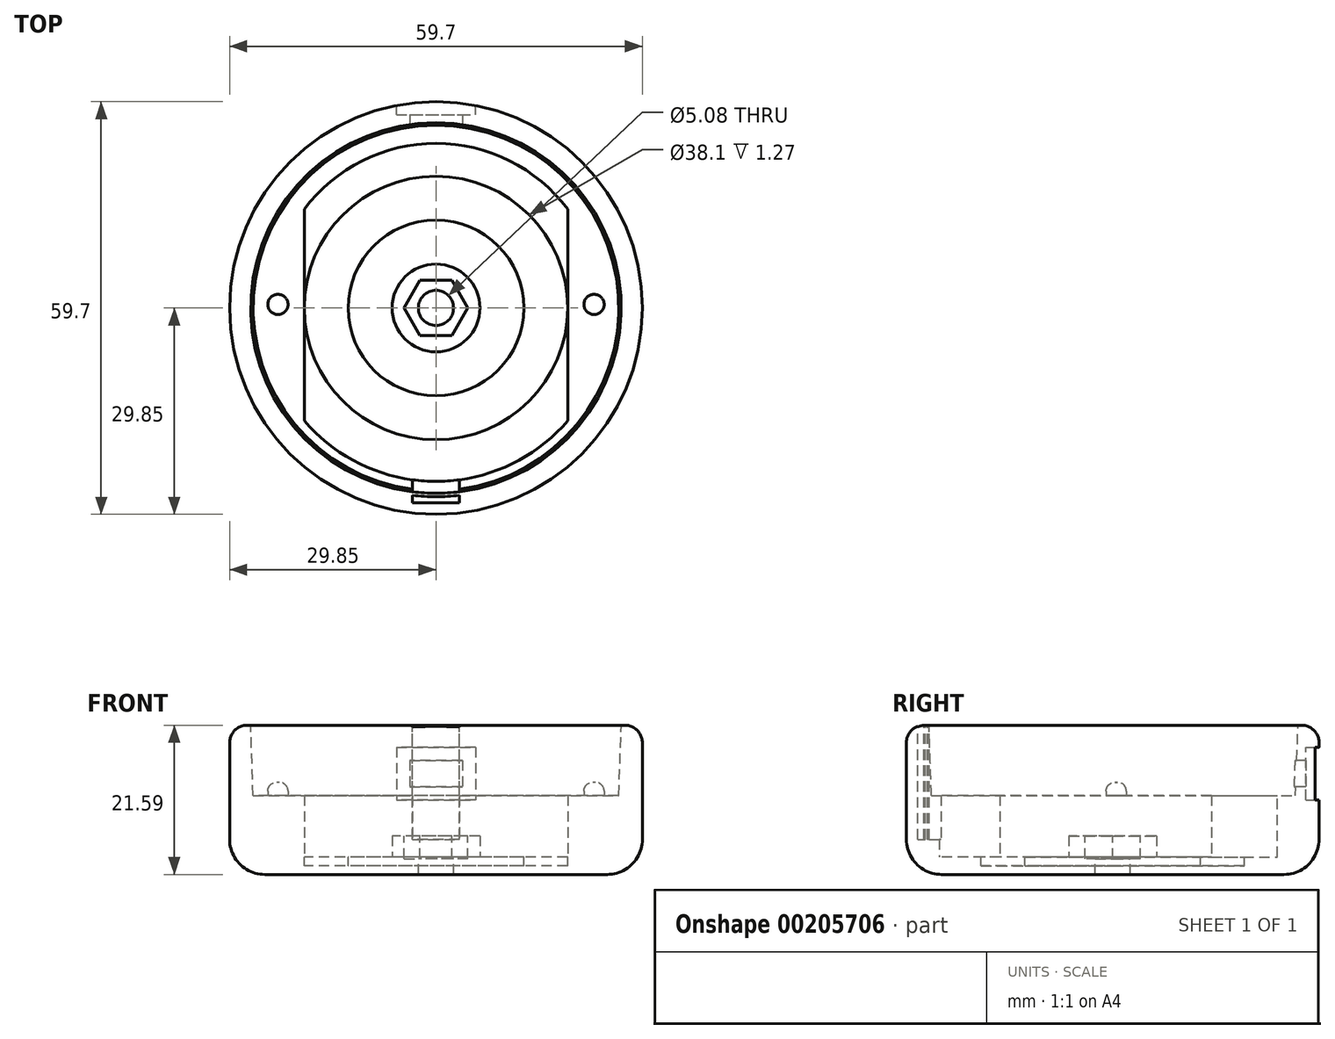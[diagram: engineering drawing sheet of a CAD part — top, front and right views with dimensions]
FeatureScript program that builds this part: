
annotation { "Feature Type Name" : "Feature", "Feature Type Description" : "" }
export const myFeature = defineFeature(function(context is Context, id is Id, definition is map)
    precondition{}
    {
        {
            var Q0;
            Q0=qCreatedBy(makeId("Top.planeOp"),FACE);
            var sketch = newSketch(context, id + "F0", { "sketchPlane" : qUnion([Q0])});
            skCircle(sketch, "E0", {"center": v(0, 0) * mm, "radius": 29.84 * mm});
            skSolve(sketch);
        }
        {
            var Q0;
            Q0 = qSketchRegion(id + "F0", true);
            extrude(context, id + "F1", {"entities" : qUnion([Q0]), "depth" : 21.59 * mm});
        }
        {
            var Q0;
            Q0=makeQuery(id+"F1.opExtrude","CAP_FACE",FACE,{"disambiguationData":[OSD([sQuery(id+"F0.wireOp",EDGE,"E0")])],"isStart":false});
            var sketch = newSketch(context, id + "F2", { "sketchPlane" : qUnion([Q0])});
            skCircle(sketch, "E1", {"center": v(0, 0) * mm, "radius": 26.8 * mm});
            skSolve(sketch);
        }
        {
            var Q0;
            Q0=makeQuery(id+"F2.imprint","IMPRINT",FACE,{"disambiguationData":[TD([[makeQuery(id+"F2.imprint","IMPRINT",EDGE,{"derivedFrom":sQuery(id+"F2.wireOp",EDGE,"E1")}),1.0]])]});
            extrude(context, id + "F3", {"entities" : qUnion([Q0]), "operationType" : NewBodyOperationType.REMOVE, "oppositeDirection" : true, "depth" : 10.16 * mm, "hasDraft" : true, "draftAngle" : 2 * degree, "draftPullDirection" : true});
        }
        {
            var Q0;
            Q0=makeQuery(id+"F3.boolean.opBoolean","COPY",FACE,{"derivedFrom":makeQuery(id+"F3.opExtrude","CAP_FACE",FACE,{"disambiguationData":[OSD([sQuery(id+"F2.wireOp",EDGE,"E1")])],"isStart":false})});
            var sketch = newSketch(context, id + "F4", { "sketchPlane" : qUnion([Q0])});
            skCircle(sketch, "E2", {"center": v(0, 0) * mm, "radius": 23.81 * mm});
            skSolve(sketch);
        }
        {
            var Q0;
            Q0 = qSketchRegion(id + "F4", true);
            extrude(context, id + "F5", {"entities" : qUnion([Q0]), "operationType" : NewBodyOperationType.REMOVE, "oppositeDirection" : true, "depth" : 8.9 * mm});
        }
        {
            var Q0;
            Q0=makeQuery(id+"F5.boolean.opBoolean","COPY",FACE,{"derivedFrom":makeQuery(id+"F5.opExtrude","CAP_FACE",FACE,{"disambiguationData":[OSD([sQuery(id+"F4.wireOp",EDGE,"E2")])],"isStart":false})});
            var sketch = newSketch(context, id + "F6", { "sketchPlane" : qUnion([Q0])});
            skCircle(sketch, "E3", {"center": v(0, 0) * mm, "radius": 6.35 * mm});
            skSolve(sketch);
        }
        {
            var Q0;
            Q0 = qSketchRegion(id + "F6", true);
            extrude(context, id + "F7", {"entities" : qUnion([Q0]), "operationType" : NewBodyOperationType.ADD, "depth" : 3.05 * mm});
        }
        {
            var Q0;
            Q0=makeQuery(id+"F7.opExtrude","CAP_FACE",FACE,{"disambiguationData":[OSD([sQuery(id+"F6.wireOp",EDGE,"E3")])],"isStart":false});
            var sketch = newSketch(context, id + "F8", { "sketchPlane" : qUnion([Q0])});
            skCircle(sketch, "E4", {"center": v(0, 0) * mm, "radius": 2.54 * mm});
            skSolve(sketch);
        }
        {
            var Q0;
            Q0=makeQuery(id+"F8.imprint","IMPRINT",FACE,{"disambiguationData":[TD([[makeQuery(id+"F8.imprint","IMPRINT",EDGE,{"derivedFrom":sQuery(id+"F8.wireOp",EDGE,"E4")}),1.0]])]});
            extrude(context, id + "F9", {"entities" : qUnion([Q0]), "operationType" : NewBodyOperationType.REMOVE, "oppositeDirection" : true, "depth" : 25.4 * mm});
        }
        {
            var Q0;
            Q0=makeQuery(id+"F7.opExtrude","CAP_FACE",FACE,{"disambiguationData":[OSD([sQuery(id+"F6.wireOp",EDGE,"E3")])],"isStart":false});
            cPlane(context, id + "F10", {"entities" : qUnion([Q0]), "cplaneType" : CPlaneType.OFFSET, "offset" : 0 * mm, "oppositeDirection" : true, "width" : 152.4 * mm, "height" : 152.4 * mm});
        }
        {
            var Q0;
            Q0=qCreatedBy(id+"F10.planeOp",FACE);
            var sketch = newSketch(context, id + "F11", { "sketchPlane" : qUnion([Q0])});
            skCircle(sketch, "E5.cCircle", {"center": v(0, 0) * mm, "radius": 4.62 * mm, "construction": true});
            skLineSegment(sketch, "E5.0", {"start": v(2.3, -4) * mm, "end": v(-2.3, -4) * mm});
            skLineSegment(sketch, "E5.1", {"start": v(-2.3, -4) * mm, "end": v(-4.62, 0) * mm});
            skLineSegment(sketch, "E5.2", {"start": v(-4.62, 0) * mm, "end": v(-2.3, 4) * mm});
            skLineSegment(sketch, "E5.3", {"start": v(-2.3, 4) * mm, "end": v(2.3, 4) * mm});
            skLineSegment(sketch, "E5.4", {"start": v(2.3, 4) * mm, "end": v(4.62, 0) * mm});
            skLineSegment(sketch, "E5.5", {"start": v(4.62, 0) * mm, "end": v(2.3, -4) * mm});
            skSolve(sketch);
        }
        {
            var Q0;
            Q0 = qSketchRegion(id + "F11", true);
            extrude(context, id + "F12", {"entities" : qUnion([Q0]), "operationType" : NewBodyOperationType.REMOVE, "oppositeDirection" : true, "depth" : 3.3 * mm});
        }
        {
            var Q0;
            Q0=makeQuery(id+"F1.opExtrude","CAP_EDGE",EDGE,{"disambiguationData":[OSD([sQuery(id+"F0.wireOp",EDGE,"E0")])],"isStart":true});
            fillet(context, id + "F13", {"entities" : qUnion([Q0]), "radius" : 5.08 * mm, "tangentPropagation" : true, "allowEdgeOverflow" : false});
        }
        {
            var Q0;
            Q0=makeQuery(id+"F1.opExtrude","CAP_EDGE",EDGE,{"disambiguationData":[OSD([sQuery(id+"F0.wireOp",EDGE,"E0")])],"isStart":false});
            fillet(context, id + "F14", {"entities" : qUnion([Q0]), "radius" : 2.54 * mm, "tangentPropagation" : true, "allowEdgeOverflow" : false});
        }
        {
            var Q0;
            Q0=makeQuery(id+"F5.boolean.opBoolean","COPY",FACE,{"derivedFrom":makeQuery(id+"F5.opExtrude","CAP_FACE",FACE,{"disambiguationData":[OSD([sQuery(id+"F4.wireOp",EDGE,"E2")])],"isStart":false})});
            var sketch = newSketch(context, id + "F15", { "sketchPlane" : qUnion([Q0])});
            skCircle(sketch, "E6", {"center": v(0, 0) * mm, "radius": 19.05 * mm});
            skCircle(sketch, "E7", {"center": v(0, 0) * mm, "radius": 12.7 * mm});
            skSolve(sketch);
        }
        {
            var Q0;
            Q0 = qSketchRegion(id + "F15", true);
            extrude(context, id + "F16", {"entities" : qUnion([Q0]), "operationType" : NewBodyOperationType.REMOVE, "oppositeDirection" : true, "depth" : 1.27 * mm});
        }
        {
            var Q0;
            {var subQ0=sQuery(id+"F4.wireOp",EDGE,"E2");Q0=makeQuery(id+"F16.boolean.opBoolean","SPLIT",FACE,{"disambiguationData":[TD([makeQuery(id+"F5.boolean.opBoolean","COPY",FACE,{"derivedFrom":makeQuery(id+"F5.opExtrude","SWEPT_FACE",FACE,{"disambiguationData":[OSD([subQ0])]})})])],"derivedFrom":makeQuery(id+"F5.boolean.opBoolean","COPY",FACE,{"derivedFrom":makeQuery(id+"F5.opExtrude","CAP_FACE",FACE,{"disambiguationData":[OSD([subQ0])],"isStart":false})})});}
            var sketch = newSketch(context, id + "F17", { "sketchPlane" : qUnion([Q0])});
            skLineSegment(sketch, "E8", {"start": v(-19.05, 14.29) * mm, "end": v(-19.05, -14.29) * mm});
            skArc(sketch, "E9", {"start": v(-19.05, 14.29) * mm, "mid": v(-23.81, 0) * mm, "end": v(-19.05, -14.29) * mm});
            skLineSegment(sketch, "E10", {"start": v(19.05, 14.29) * mm, "end": v(19.05, -14.29) * mm});
            skArc(sketch, "E11", {"start": v(19.05, -14.29) * mm, "mid": v(23.81, 0) * mm, "end": v(19.05, 14.29) * mm});
            skSolve(sketch);
        }
        {
            var Q0;
            {var subQ0=sQuery(id+"F17.wireOp",EDGE,"E9");Q0=makeQuery(id+"F17.imprint","IMPRINT",FACE,{"disambiguationData":[TD([[makeQuery(id+"F17.imprint","IMPRINT",EDGE,{"derivedFrom":subQ0}),1.0]])]});}
            var Q1;
            {var subQ0=sQuery(id+"F17.wireOp",EDGE,"E11");Q1=makeQuery(id+"F17.imprint","IMPRINT",FACE,{"disambiguationData":[TD([[makeQuery(id+"F17.imprint","IMPRINT",EDGE,{"derivedFrom":subQ0}),1.0]])]});}
            var Q2;
            Q2=makeQuery(id+"F3.boolean.opBoolean","COPY",FACE,{"derivedFrom":makeQuery(id+"F3.opExtrude","CAP_FACE",FACE,{"disambiguationData":[OSD([sQuery(id+"F2.wireOp",EDGE,"E1")])],"isStart":false})});
            extrude(context, id + "F18", {"entities" : qUnion([Q0, Q1]), "operationType" : NewBodyOperationType.ADD, "endBound" : BoundingType.UP_TO_SURFACE, "endBoundEntityFace" : qUnion([Q2]), "depth" : 25.4 * mm});
        }
        {
            var Q0;
            {var subQ0=sQuery(id+"F2.wireOp",EDGE,"E1");Q0=makeQuery(id+"F18.boolean.opBoolean","MERGE",FACE,{"derivedFrom":[makeQuery(id+"F3.boolean.opBoolean","COPY",FACE,{"derivedFrom":makeQuery(id+"F3.opExtrude","CAP_FACE",FACE,{"disambiguationData":[OSD([subQ0])],"isStart":false})}),makeQuery(id+"F18.opExtrude","CAP_FACE",FACE,{"disambiguationData":[OSD([subQ0]),ownerDisambiguation([makeQuery(id+"F18.opExtrude","SWEPT_BODY",BODY,{"disambiguationData":[OSD([sQuery(id+"F17.wireOp",EDGE,"E8"),sQuery(id+"F17.wireOp",EDGE,"E9")])]})])],"isStart":false}),makeQuery(id+"F18.opExtrude","CAP_FACE",FACE,{"disambiguationData":[OSD([subQ0]),ownerDisambiguation([makeQuery(id+"F18.opExtrude","SWEPT_BODY",BODY,{"disambiguationData":[OSD([sQuery(id+"F17.wireOp",EDGE,"E10"),sQuery(id+"F17.wireOp",EDGE,"E11")])]})])],"isStart":false})]});}
            var sketch = newSketch(context, id + "F19", { "sketchPlane" : qUnion([Q0])});
            skCircle(sketch, "E12", {"center": v(-22.86, 0.5) * mm, "radius": 1.46 * mm});
            skCircle(sketch, "E13", {"center": v(22.86, 0.5) * mm, "radius": 1.46 * mm});
            skSolve(sketch);
        }
        {
            var Q0;
            Q0 = qSketchRegion(id + "F19", true);
            extrude(context, id + "F20", {"entities" : qUnion([Q0]), "operationType" : NewBodyOperationType.ADD, "depth" : 1.9 * mm});
        }
        {
            var Q0;
            Q0=makeQuery(id+"F20.opExtrude","CAP_EDGE",EDGE,{"disambiguationData":[OSD([sQuery(id+"F19.wireOp",EDGE,"E12")])],"isStart":false});
            var Q1;
            Q1=makeQuery(id+"F20.opExtrude","CAP_EDGE",EDGE,{"disambiguationData":[OSD([sQuery(id+"F19.wireOp",EDGE,"E13")])],"isStart":false});
            fillet(context, id + "F21", {"entities" : qUnion([Q0, Q1]), "radius" : 1.27 * mm, "tangentPropagation" : true, "allowEdgeOverflow" : false});
        }
        {
            var Q0;
            Q0=qCreatedBy(makeId("Front.planeOp"),FACE);
            var sketch = newSketch(context, id + "F22", { "sketchPlane" : qUnion([Q0])});
            skLineSegment(sketch, "E14.bottom", {"start": v(3.8, 12.7) * mm, "end": v(-3.81, 12.7) * mm});
            skLineSegment(sketch, "E14.top", {"start": v(3.8, 16.51) * mm, "end": v(-3.81, 16.51) * mm});
            skLineSegment(sketch, "E14.left", {"start": v(3.8, 12.7) * mm, "end": v(3.8, 16.51) * mm});
            skLineSegment(sketch, "E14.right", {"start": v(-3.81, 12.7) * mm, "end": v(-3.81, 16.51) * mm});
            skPoint(sketch, "E14.middle", {"position": v(0, 14.6) * mm});
            skSolve(sketch);
        }
        {
            var Q0;
            Q0=makeQuery(id+"F22.imprint","IMPRINT",FACE,{"disambiguationData":[TD([[makeQuery(id+"F22.imprint","IMPRINT",EDGE,{"derivedFrom":sQuery(id+"F22.wireOp",EDGE,"E14.bottom")}),-1.0]])]});
            extrude(context, id + "F23", {"entities" : qUnion([Q0]), "operationType" : NewBodyOperationType.REMOVE, "oppositeDirection" : true, "depth" : 36.58 * mm});
        }
        {
            var Q0;
            Q0=makeQuery(id+"F1.opExtrude","CAP_FACE",FACE,{"disambiguationData":[OSD([sQuery(id+"F0.wireOp",EDGE,"E0")])],"isStart":false});
            var sketch = newSketch(context, id + "F24", { "sketchPlane" : qUnion([Q0])});
            skLineSegment(sketch, "E15.bottom", {"start": v(3.4, -28.2) * mm, "end": v(-3.4, -28.2) * mm});
            skLineSegment(sketch, "E15.top", {"start": v(3.4, -23.13) * mm, "end": v(-3.4, -23.13) * mm});
            skLineSegment(sketch, "E15.left", {"start": v(3.4, -28.2) * mm, "end": v(3.4, -23.13) * mm});
            skLineSegment(sketch, "E15.right", {"start": v(-3.4, -28.2) * mm, "end": v(-3.4, -23.13) * mm});
            skPoint(sketch, "E15.middle", {"position": v(0, -25.67) * mm});
            skSolve(sketch);
        }
        {
            var Q0;
            {var subQ0=sQuery(id+"F24.wireOp",EDGE,"E15.top");Q0=makeQuery(id+"F24.imprint","IMPRINT",FACE,{"disambiguationData":[TD([[makeQuery(id+"F24.imprint","IMPRINT",EDGE,{"derivedFrom":subQ0}),1.0]])]});}
            var Q1;
            {var subQ0=sQuery(id+"F24.wireOp",EDGE,"E15.bottom");Q1=makeQuery(id+"F24.imprint","IMPRINT",FACE,{"disambiguationData":[TD([[makeQuery(id+"F24.imprint","IMPRINT",EDGE,{"derivedFrom":subQ0}),-1.0]])]});}
            var Q2;
            {var subQ0=sQuery(id+"F24.wireOp",EDGE,"E15.left");var subQ4=makeQuery(id+"F3.boolean.opBoolean","COPY",EDGE,{"derivedFrom":makeQuery(id+"F3.opExtrude","CAP_EDGE",EDGE,{"disambiguationData":[OSD([sQuery(id+"F2.wireOp",EDGE,"E1")])],"isStart":true})});var subQ5=makeQuery(id+"F24.imprint","INTERSECT",VERTEX,{"derivedFrom":[subQ4,subQ0]});Q2=makeQuery(id+"F24.imprint","IMPRINT",FACE,{"disambiguationData":[TD([[makeQuery(id+"F24.imprint","IMPRINT",EDGE,{"disambiguationData":[TD([[subQ5,1.0]])],"derivedFrom":subQ4}),-1.0]])]});}
            extrude(context, id + "F25", {"entities" : qUnion([Q0, Q1, Q2]), "operationType" : NewBodyOperationType.REMOVE, "oppositeDirection" : true, "depth" : 16.5 * mm});
        }
        {
            var Q0;
            {var subQ0=sQuery(id+"F4.wireOp",EDGE,"E2");Q0=makeQuery(id+"F18.boolean.opBoolean","SPLIT",FACE,{"disambiguationData":[OD(1.0)],"derivedFrom":makeQuery(id+"F16.boolean.opBoolean","SPLIT",FACE,{"disambiguationData":[TD([makeQuery(id+"F5.boolean.opBoolean","COPY",FACE,{"derivedFrom":makeQuery(id+"F5.opExtrude","SWEPT_FACE",FACE,{"disambiguationData":[OSD([subQ0])]})})])],"derivedFrom":makeQuery(id+"F5.boolean.opBoolean","COPY",FACE,{"derivedFrom":makeQuery(id+"F5.opExtrude","CAP_FACE",FACE,{"disambiguationData":[OSD([subQ0])],"isStart":false})})})});}
            var sketch = newSketch(context, id + "F26", { "sketchPlane" : qUnion([Q0])});
            skArc(sketch, "E16", {"start": v(-19.05, -14.29) * mm, "mid": v(0, -23.81) * mm, "end": v(19.05, -14.29) * mm});
            skLineSegment(sketch, "E17", {"start": v(19.05, -14.29) * mm, "end": v(19.05, -16.32) * mm});
            skLineSegment(sketch, "E18", {"start": v(-19.05, -14.29) * mm, "end": v(-19.05, -16.32) * mm});
            skArc(sketch, "E19", {"start": v(-19.05, -16.32) * mm, "mid": v(0, -25.08) * mm, "end": v(19.05, -16.32) * mm});
            skSolve(sketch);
        }
        {
            var Q0;
            Q0 = qSketchRegion(id + "F26", true);
            extrude(context, id + "F27", {"entities" : qUnion([Q0]), "operationType" : NewBodyOperationType.REMOVE, "endBound" : BoundingType.THROUGH_ALL, "depth" : 5.08 * mm});
        }
        {
            var Q0;
            Q0=qCreatedBy(makeId("Front.planeOp"),FACE);
            cPlane(context, id + "F28", {"entities" : qUnion([Q0]), "cplaneType" : CPlaneType.OFFSET, "offset" : 31.75 * mm, "oppositeDirection" : true, "width" : 152.4 * mm, "height" : 152.4 * mm});
        }
        {
            var Q0;
            Q0=qCreatedBy(id+"F28.planeOp",FACE);
            var sketch = newSketch(context, id + "F29", { "sketchPlane" : qUnion([Q0])});
            skLineSegment(sketch, "E20.bottom", {"start": v(-5.72, 10.8) * mm, "end": v(5.72, 10.8) * mm});
            skLineSegment(sketch, "E20.top", {"start": v(-5.72, 18.41) * mm, "end": v(5.72, 18.41) * mm});
            skLineSegment(sketch, "E20.left", {"start": v(-5.72, 10.8) * mm, "end": v(-5.72, 18.41) * mm});
            skLineSegment(sketch, "E20.right", {"start": v(5.72, 10.8) * mm, "end": v(5.72, 18.41) * mm});
            skPoint(sketch, "E20.middle", {"position": v(0, 14.6) * mm});
            skSolve(sketch);
        }
        {
            var Q0;
            Q0 = qSketchRegion(id + "F29", true);
            extrude(context, id + "F30", {"entities" : qUnion([Q0]), "operationType" : NewBodyOperationType.REMOVE, "depth" : 3.8 * mm});
        }
    });
